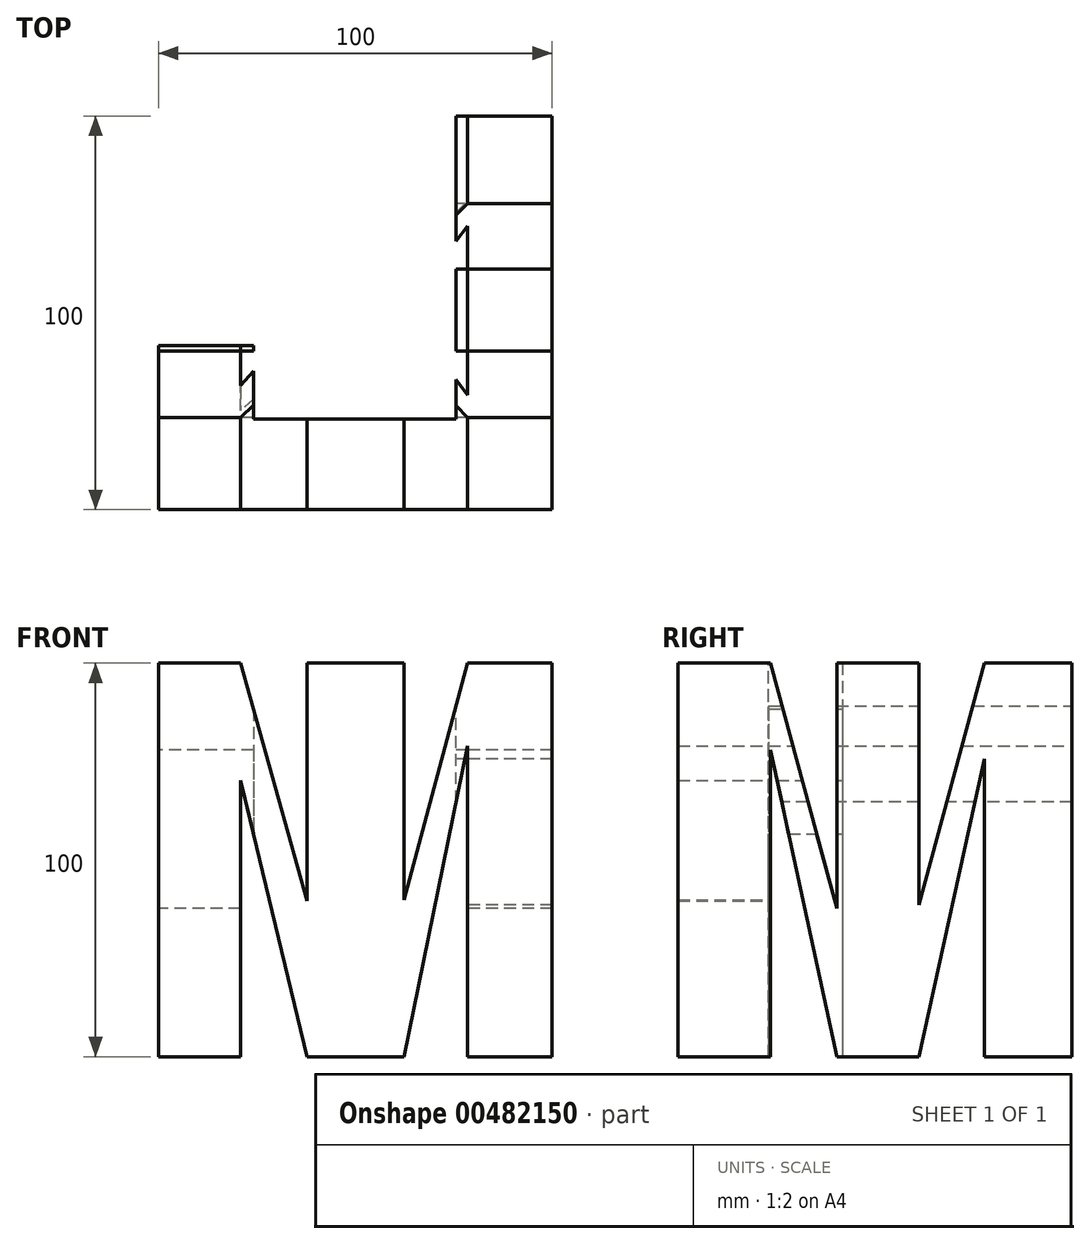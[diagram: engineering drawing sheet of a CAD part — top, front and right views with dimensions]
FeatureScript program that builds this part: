
annotation { "Feature Type Name" : "Feature", "Feature Type Description" : "" }
export const myFeature = defineFeature(function(context is Context, id is Id, definition is map)
    precondition{}
    {
        {
            var Q0;
            Q0=qCreatedBy(makeId("Top.planeOp"),FACE);
            var sketch = newSketch(context, id + "F0", { "sketchPlane" : qUnion([Q0])});
            skLineSegment(sketch, "E0.bottom", {"start": v(50, 50) * mm, "end": v(-50, 50) * mm, "construction": true});
            skLineSegment(sketch, "E0.top", {"start": v(50, -50) * mm, "end": v(-50, -50) * mm, "construction": true});
            skLineSegment(sketch, "E0.left", {"start": v(50, 50) * mm, "end": v(50, -50) * mm, "construction": true});
            skLineSegment(sketch, "E0.right", {"start": v(-50, 50) * mm, "end": v(-50, -50) * mm, "construction": true});
            skPoint(sketch, "E0.middle", {"position": v(0, 0) * mm});
            skLineSegment(sketch, "E1.bottom", {"start": v(50, 50) * mm, "end": v(25.55, 50) * mm});
            skLineSegment(sketch, "E1.top", {"start": v(50, -50) * mm, "end": v(25.55, -50) * mm});
            skLineSegment(sketch, "E1.left", {"start": v(50, 50) * mm, "end": v(50, -50) * mm});
            skLineSegment(sketch, "E1.right", {"start": v(25.55, 50) * mm, "end": v(25.55, -27.04) * mm});
            skLineSegment(sketch, "E2.bottom", {"start": v(25.55, -27.04) * mm, "end": v(-25.93, -27.04) * mm});
            skLineSegment(sketch, "E2.top", {"start": v(50, -50) * mm, "end": v(-50, -50) * mm});
            skLineSegment(sketch, "E2.left", {"start": v(50, -27.04) * mm, "end": v(50, -50) * mm});
            skLineSegment(sketch, "E2.right", {"start": v(-50, -27.04) * mm, "end": v(-50, -50) * mm});
            skLineSegment(sketch, "E3.bottom", {"start": v(-50, -50) * mm, "end": v(-25.93, -50) * mm});
            skLineSegment(sketch, "E3.top", {"start": v(-50, -8.3) * mm, "end": v(-25.93, -8.3) * mm});
            skLineSegment(sketch, "E3.left", {"start": v(-50, -50) * mm, "end": v(-50, -8.3) * mm});
            skLineSegment(sketch, "E3.right", {"start": v(-25.93, -27.04) * mm, "end": v(-25.93, -8.3) * mm});
            skSolve(sketch);
        }
        {
            var Q0;
            Q0=qCreatedBy(makeId("Front.planeOp"),FACE);
            var sketch = newSketch(context, id + "F1", { "sketchPlane" : qUnion([Q0])});
            skLineSegment(sketch, "E4.bottom", {"start": v(50, 50) * mm, "end": v(-50, 50) * mm, "construction": true});
            skLineSegment(sketch, "E4.top", {"start": v(50, -50) * mm, "end": v(-50, -50) * mm, "construction": true});
            skLineSegment(sketch, "E4.left", {"start": v(50, 50) * mm, "end": v(50, -50) * mm, "construction": true});
            skLineSegment(sketch, "E4.right", {"start": v(-50, 50) * mm, "end": v(-50, -50) * mm, "construction": true});
            skPoint(sketch, "E4.middle", {"position": v(0, 0) * mm});
            skLineSegment(sketch, "E5.bottom", {"start": v(-50, 50) * mm, "end": v(-29.18, 50) * mm});
            skLineSegment(sketch, "E5.top", {"start": v(-50, -50) * mm, "end": v(-29.18, -50) * mm});
            skLineSegment(sketch, "E5.left", {"start": v(-50, 50) * mm, "end": v(-50, -50) * mm});
            skLineSegment(sketch, "E5.right", {"start": v(-29.18, 20.16) * mm, "end": v(-29.18, -50) * mm});
            skLineSegment(sketch, "E6.bottom", {"start": v(50, 50) * mm, "end": v(28.46, 50) * mm});
            skLineSegment(sketch, "E6.top", {"start": v(50, -50) * mm, "end": v(28.46, -50) * mm});
            skLineSegment(sketch, "E6.left", {"start": v(50, 50) * mm, "end": v(50, -50) * mm});
            skLineSegment(sketch, "E6.right", {"start": v(28.46, 28.94) * mm, "end": v(28.46, -50) * mm});
            skLineSegment(sketch, "E7.bottom", {"start": v(-12.33, 50) * mm, "end": v(12.33, 50) * mm});
            skLineSegment(sketch, "E7.top", {"start": v(-12.33, -50) * mm, "end": v(12.33, -50) * mm});
            skLineSegment(sketch, "E7.left", {"start": v(-12.33, 50) * mm, "end": v(-12.33, -10.44) * mm});
            skLineSegment(sketch, "E7.right", {"start": v(12.33, 50) * mm, "end": v(12.33, -10.2) * mm});
            skLineSegment(sketch, "E8", {"start": v(-29.18, 20.16) * mm, "end": v(-12.33, -50) * mm});
            skLineSegment(sketch, "E9", {"start": v(-29.18, 50) * mm, "end": v(-12.33, -10.44) * mm});
            skLineSegment(sketch, "E10", {"start": v(12.33, -50) * mm, "end": v(28.46, 28.94) * mm});
            skLineSegment(sketch, "E11", {"start": v(28.46, 50) * mm, "end": v(12.33, -10.2) * mm});
            skSolve(sketch);
        }
        {
            var Q0;
            Q0=qCreatedBy(makeId("Right.planeOp"),FACE);
            var sketch = newSketch(context, id + "F2", { "sketchPlane" : qUnion([Q0])});
            skLineSegment(sketch, "E12.bottom", {"start": v(50, 50) * mm, "end": v(-50, 50) * mm, "construction": true});
            skLineSegment(sketch, "E12.top", {"start": v(50, -50) * mm, "end": v(-50, -50) * mm, "construction": true});
            skLineSegment(sketch, "E12.left", {"start": v(50, 50) * mm, "end": v(50, -50) * mm, "construction": true});
            skLineSegment(sketch, "E12.right", {"start": v(-50, 50) * mm, "end": v(-50, -50) * mm, "construction": true});
            skPoint(sketch, "E12.middle", {"position": v(0, 0) * mm});
            skLineSegment(sketch, "E13.bottom", {"start": v(-50, 50) * mm, "end": v(-26.57, 50) * mm});
            skLineSegment(sketch, "E13.top", {"start": v(-50, -50) * mm, "end": v(-26.57, -50) * mm});
            skLineSegment(sketch, "E13.left", {"start": v(-50, 50) * mm, "end": v(-50, -50) * mm});
            skLineSegment(sketch, "E13.right", {"start": v(-26.57, 27.99) * mm, "end": v(-26.57, -50) * mm});
            skLineSegment(sketch, "E14.bottom", {"start": v(50, 50) * mm, "end": v(27.75, 50) * mm});
            skLineSegment(sketch, "E14.top", {"start": v(50, -50) * mm, "end": v(27.75, -50) * mm});
            skLineSegment(sketch, "E14.left", {"start": v(50, 50) * mm, "end": v(50, -50) * mm});
            skLineSegment(sketch, "E14.right", {"start": v(27.75, 25.62) * mm, "end": v(27.75, -50) * mm});
            skLineSegment(sketch, "E15.bottom", {"start": v(-9.73, 50) * mm, "end": v(11.15, 50) * mm});
            skLineSegment(sketch, "E15.top", {"start": v(-9.73, -50) * mm, "end": v(11.15, -50) * mm});
            skLineSegment(sketch, "E15.left", {"start": v(-9.73, 50) * mm, "end": v(-9.73, -12.33) * mm});
            skLineSegment(sketch, "E15.right", {"start": v(11.15, 50) * mm, "end": v(11.15, -11.39) * mm});
            skLineSegment(sketch, "E16", {"start": v(-26.57, 27.99) * mm, "end": v(-9.73, -50) * mm});
            skLineSegment(sketch, "E17", {"start": v(-26.57, 50) * mm, "end": v(-9.73, -12.33) * mm});
            skLineSegment(sketch, "E18", {"start": v(27.75, 25.62) * mm, "end": v(11.15, -50) * mm});
            skLineSegment(sketch, "E19", {"start": v(27.75, 50) * mm, "end": v(11.15, -11.39) * mm});
            skSolve(sketch);
        }
        {
            var Q0;
            Q0 = qSketchRegion(id + "F0", true);
            extrude(context, id + "F3", {"entities" : qUnion([Q0]), "endBound" : BoundingType.SYMMETRIC, "depth" : 100 * mm});
        }
        {
            var Q0;
            Q0 = qSketchRegion(id + "F1", true);
            extrude(context, id + "F4", {"entities" : qUnion([Q0]), "operationType" : NewBodyOperationType.INTERSECT, "endBound" : BoundingType.SYMMETRIC, "depth" : 100 * mm});
        }
        {
            var Q0;
            Q0 = qSketchRegion(id + "F2", true);
            extrude(context, id + "F5", {"entities" : qUnion([Q0]), "operationType" : NewBodyOperationType.INTERSECT, "endBound" : BoundingType.SYMMETRIC, "depth" : 100 * mm});
        }
    });
